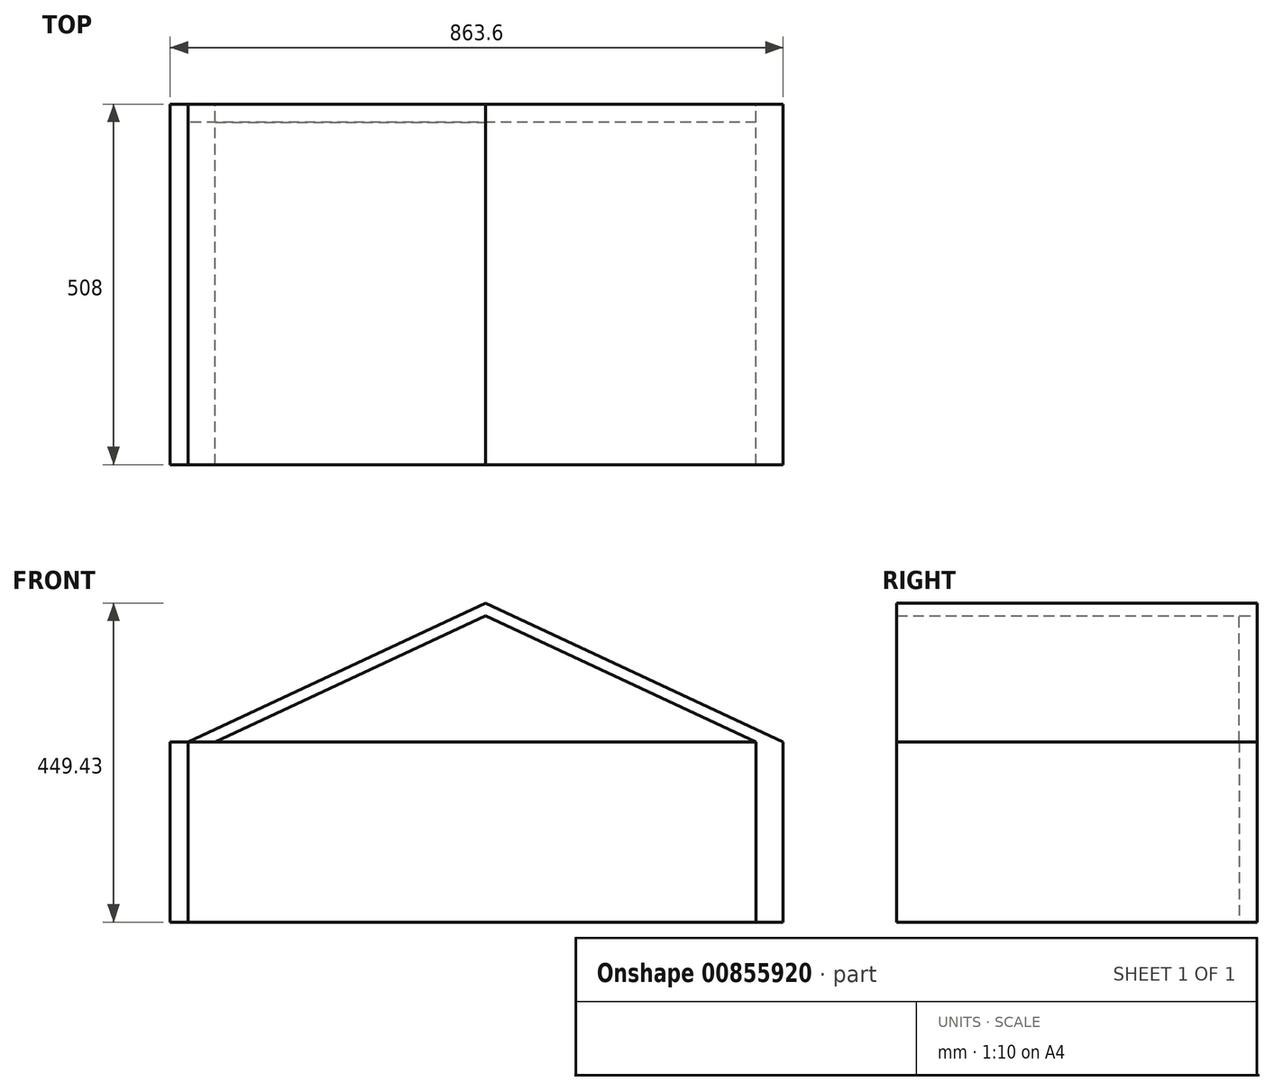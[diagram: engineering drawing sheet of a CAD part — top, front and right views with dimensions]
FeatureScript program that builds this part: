
annotation { "Feature Type Name" : "Feature", "Feature Type Description" : "" }
export const myFeature = defineFeature(function(context is Context, id is Id, definition is map)
    precondition{}
    {
        {
            var Q0;
            Q0=qCreatedBy(makeId("Front.planeOp"),FACE);
            var sketch = newSketch(context, id + "F0", { "sketchPlane" : qUnion([Q0])});
            skLineSegment(sketch, "E0", {"start": v(0, 117.3) * mm, "end": v(0, -136.7) * mm});
            skLineSegment(sketch, "E1", {"start": v(0, -136.7) * mm, "end": v(-25.4, -136.7) * mm});
            skLineSegment(sketch, "E2", {"start": v(-25.4, -136.7) * mm, "end": v(-25.4, 117.3) * mm});
            skLineSegment(sketch, "E3", {"start": v(-25.4, 117.3) * mm, "end": v(0, 117.3) * mm});
            skLineSegment(sketch, "E4", {"start": v(0, -136.7) * mm, "end": v(76.2, -136.7) * mm});
            skLineSegment(sketch, "E5", {"start": v(76.2, -136.7) * mm, "end": v(838.2, -136.7) * mm});
            skLineSegment(sketch, "E6", {"start": v(838.2, -136.7) * mm, "end": v(838.2, 117.3) * mm});
            skLineSegment(sketch, "E7", {"start": v(838.2, 117.3) * mm, "end": v(0, 117.3) * mm});
            skLineSegment(sketch, "E8", {"start": v(0, 117.3) * mm, "end": v(419.1, 312.72) * mm});
            skLineSegment(sketch, "E9", {"start": v(419.1, 312.72) * mm, "end": v(838.2, 117.3) * mm});
            skLineSegment(sketch, "E10", {"start": v(800.1, 117.3) * mm, "end": v(800.1, -136.7) * mm});
            skLineSegment(sketch, "E11", {"start": v(0, 117.3) * mm, "end": v(38.1, 117.3) * mm});
            skLineSegment(sketch, "E12", {"start": v(38.1, 117.3) * mm, "end": v(419.1, 294.95) * mm});
            skLineSegment(sketch, "E13", {"start": v(800.1, 117.3) * mm, "end": v(419.1, 294.95) * mm});
            skLineSegment(sketch, "E14", {"start": v(-470.83, 117.3) * mm, "end": v(-470.83, -136.7) * mm});
            skLineSegment(sketch, "E15", {"start": v(-470.83, 117.3) * mm, "end": v(-508.93, 117.3) * mm});
            skLineSegment(sketch, "E16", {"start": v(-508.93, 117.3) * mm, "end": v(-508.93, -136.7) * mm});
            skLineSegment(sketch, "E17", {"start": v(-508.93, -136.7) * mm, "end": v(-470.83, -136.7) * mm});
            skLineSegment(sketch, "E18", {"start": v(-330.2, 117.3) * mm, "end": v(-330.2, -136.7) * mm});
            skLineSegment(sketch, "E19", {"start": v(-330.2, -136.7) * mm, "end": v(-470.83, -136.7) * mm});
            skLineSegment(sketch, "E20", {"start": v(-330.2, 117.3) * mm, "end": v(-470.83, 117.3) * mm});
            skLineSegment(sketch, "E21", {"start": v(-330.2, 117.3) * mm, "end": v(-25.4, 117.3) * mm});
            skLineSegment(sketch, "E22", {"start": v(-25.4, -136.7) * mm, "end": v(-330.2, -136.7) * mm});
            skSolve(sketch);
        }
        {
            var Q0;
            Q0=makeQuery(id+"F0.imprint","IMPRINT",FACE,{"disambiguationData":[TD([[makeQuery(id+"F0.imprint","IMPRINT",EDGE,{"derivedFrom":sQuery(id+"F0.wireOp",EDGE,"E0")}),-1.0]])]});
            extrude(context, id + "F1", {"entities" : qUnion([Q0]), "depth" : 508 * mm, "offsetDistance" : 25.4 * mm});
        }
        {
            var Q0;
            {var subQ0=sQuery(id+"F0.wireOp",EDGE,"E6");Q0=makeQuery(id+"F0.imprint","IMPRINT",FACE,{"disambiguationData":[TD([[makeQuery(id+"F0.imprint","IMPRINT",EDGE,{"derivedFrom":subQ0}),1.0]])]});}
            extrude(context, id + "F2", {"entities" : qUnion([Q0]), "depth" : 508 * mm, "offsetDistance" : 25.4 * mm});
        }
        {
            var Q0;
            Q0=makeQuery(id+"F0.imprint","IMPRINT",FACE,{"disambiguationData":[TD([[makeQuery(id+"F0.imprint","IMPRINT",EDGE,{"derivedFrom":sQuery(id+"F0.wireOp",EDGE,"E8")}),-1.0]])]});
            extrude(context, id + "F3", {"entities" : qUnion([Q0]), "operationType" : NewBodyOperationType.ADD, "depth" : 508 * mm, "offsetDistance" : 25.4 * mm});
        }
        {
            var Q0;
            Q0=makeQuery(id+"F0.imprint","IMPRINT",FACE,{"disambiguationData":[TD([[makeQuery(id+"F0.imprint","IMPRINT",EDGE,{"derivedFrom":sQuery(id+"F0.wireOp",EDGE,"E0")}),1.0]])]});
            extrude(context, id + "F4", {"entities" : qUnion([Q0]), "depth" : 25.4 * mm, "offsetDistance" : 25.4 * mm});
        }
        {
            var Q0;
            {var subQ0=sQuery(id+"F0.wireOp",EDGE,"E12");Q0=makeQuery(id+"F0.imprint","IMPRINT",FACE,{"disambiguationData":[TD([[makeQuery(id+"F0.imprint","IMPRINT",EDGE,{"derivedFrom":subQ0}),-1.0]])]});}
            extrude(context, id + "F5", {"entities" : qUnion([Q0]), "depth" : 25.4 * mm, "offsetDistance" : 25.4 * mm});
        }
    });
